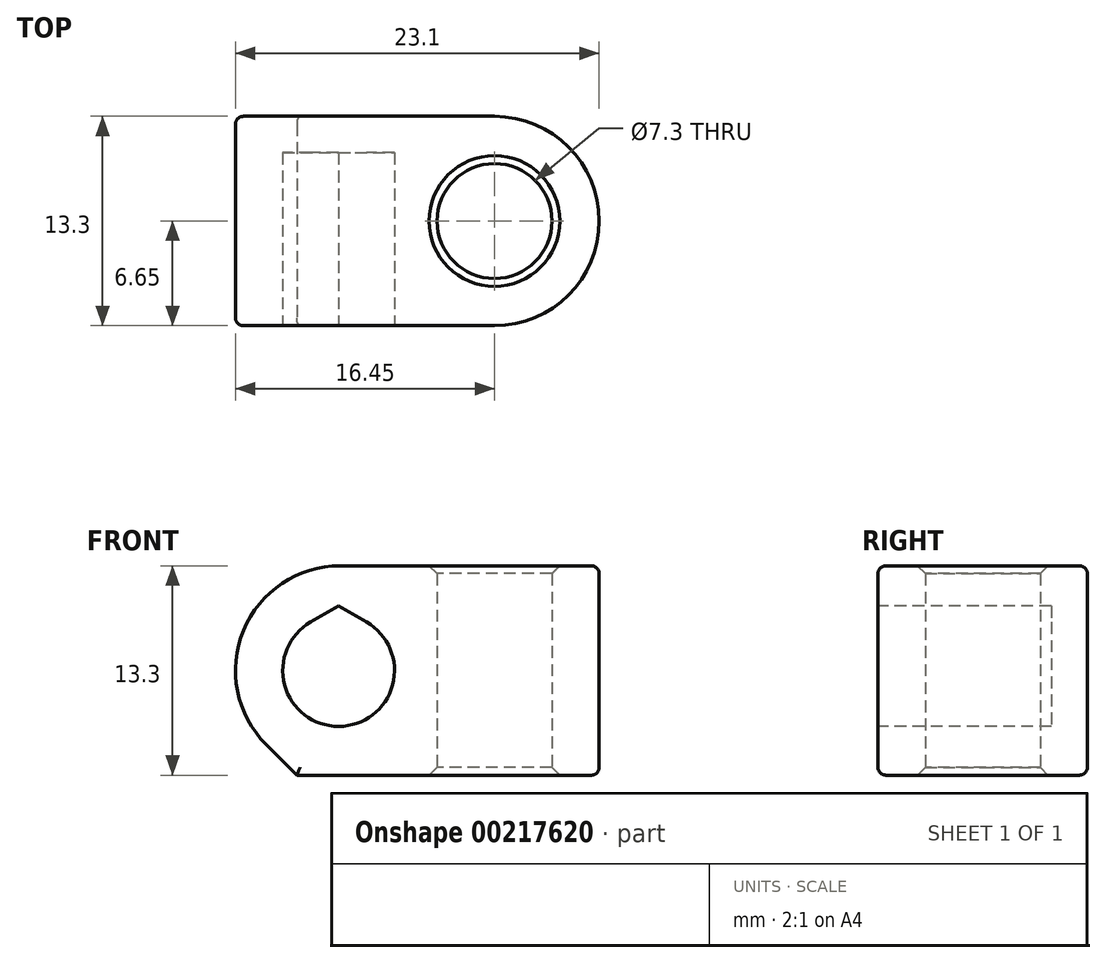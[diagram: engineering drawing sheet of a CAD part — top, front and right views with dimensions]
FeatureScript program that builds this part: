
annotation { "Feature Type Name" : "Feature", "Feature Type Description" : "" }
export const myFeature = defineFeature(function(context is Context, id is Id, definition is map)
    precondition{}
    {
        {
            var Q0;
            Q0=qCreatedBy(makeId("Top.planeOp"),FACE);
            var sketch = newSketch(context, id + "F0", { "sketchPlane" : qUnion([Q0])});
            skCircle(sketch, "E0", {"center": v(0, 0) * mm, "radius": 3.65 * mm});
            skLineSegment(sketch, "E1", {"start": v(-3.65, 0) * mm, "end": v(-6.15, 0) * mm, "construction": true});
            skCircle(sketch, "E2", {"center": v(-9.8, 0) * mm, "radius": 3.65 * mm});
            skLineSegment(sketch, "E3", {"start": v(0, 3.65) * mm, "end": v(0, 6.65) * mm, "construction": true});
            skLineSegment(sketch, "E4", {"start": v(0, 6.65) * mm, "end": v(-16.45, 6.65) * mm});
            skLineSegment(sketch, "E5", {"start": v(0, -6.65) * mm, "end": v(-16.45, -6.65) * mm});
            skLineSegment(sketch, "E6", {"start": v(-16.45, -6.65) * mm, "end": v(-16.45, 6.65) * mm});
            skLineSegment(sketch, "E7", {"start": v(-13.45, 0) * mm, "end": v(-16.45, 0) * mm, "construction": true});
            skArc(sketch, "E8.trimOffspring", {"start": v(0, -6.65) * mm, "mid": v(6.65, 0) * mm, "end": v(0, 6.65) * mm});
            skSolve(sketch);
        }
        {
            var Q0;
            Q0=makeQuery(id+"F0.imprint","IMPRINT",FACE,{"disambiguationData":[TD([[makeQuery(id+"F0.imprint","IMPRINT",EDGE,{"derivedFrom":sQuery(id+"F0.wireOp",EDGE,"E0")}),-1.0]])]});
            var Q1;
            Q1=makeQuery(id+"F0.imprint","IMPRINT",FACE,{"disambiguationData":[TD([[makeQuery(id+"F0.imprint","IMPRINT",EDGE,{"derivedFrom":sQuery(id+"F0.wireOp",EDGE,"E2")}),1.0]])]});
            extrude(context, id + "F1", {"entities" : qUnion([Q0, Q1]), "depth" : 13.3 * mm});
        }
        {
            var Q0;
            Q0=makeQuery(id+"F1.opExtrude","SWEPT_FACE",FACE,{"disambiguationData":[OSD([sQuery(id+"F0.wireOp",EDGE,"E5")])]});
            var sketch = newSketch(context, id + "F2", { "sketchPlane" : qUnion([Q0])});
            skLineSegment(sketch, "E9", {"start": v(-16.45, 6.65) * mm, "end": v(-13.45, 6.65) * mm, "construction": true});
            skArc(sketch, "E10", {"start": v(-11.67, 9.72) * mm, "mid": v(-9.9, 3.1) * mm, "end": v(-8.12, 9.72) * mm});
            skLineSegment(sketch, "E11", {"start": v(-9.9, 6.65) * mm, "end": v(-9.9, 10.75) * mm, "construction": true});
            skLineSegment(sketch, "E12", {"start": v(-9.9, 10.75) * mm, "end": v(-11.67, 9.72) * mm});
            skLineSegment(sketch, "E13", {"start": v(-9.9, 10.75) * mm, "end": v(-8.12, 9.72) * mm});
            skSolve(sketch);
        }
        {
            var Q0;
            Q0=makeQuery(id+"F2.imprint","IMPRINT",FACE,{"disambiguationData":[TD([[makeQuery(id+"F2.imprint","IMPRINT",EDGE,{"derivedFrom":sQuery(id+"F2.wireOp",EDGE,"E10")}),1.0]])]});
            extrude(context, id + "F3", {"entities" : qUnion([Q0]), "operationType" : NewBodyOperationType.REMOVE, "oppositeDirection" : true, "depth" : 11 * mm});
        }
        {
            var Q0;
            Q0=makeQuery(id+"F1.opExtrude","CAP_EDGE",EDGE,{"disambiguationData":[OSD([sQuery(id+"F0.wireOp",EDGE,"E6")])],"isStart":false});
            fillet(context, id + "F4", {"entities" : qUnion([Q0]), "radius" : 6.65 * mm, "tangentPropagation" : true, "allowEdgeOverflow" : false});
        }
        {
            var Q0;
            Q0=makeQuery(id+"F1.opExtrude","SWEPT_FACE",FACE,{"disambiguationData":[OSD([sQuery(id+"F0.wireOp",EDGE,"E5")])]});
            var sketch = newSketch(context, id + "F5", { "sketchPlane" : qUnion([Q0])});
            skLineSegment(sketch, "E14", {"start": v(-16.45, 6.65) * mm, "end": v(-16.45, 6.65) * mm});
            skLineSegment(sketch, "E15", {"start": v(-9.8, 0) * mm, "end": v(-3.62, 0) * mm});
            skPoint(sketch, "E16.visualSharp", {"position": v(-16.45, 0) * mm});
            skArc(sketch, "E16.filletArc", {"start": v(-16.45, 6.65) * mm, "mid": v(-15.94, 4.1) * mm, "end": v(-14.5, 1.95) * mm});
            skLineSegment(sketch, "E17", {"start": v(-14.5, 1.95) * mm, "end": v(-12.55, 0) * mm});
            skSolve(sketch);
        }
        {
            var Q0;
            Q0=makeQuery(id+"F5.imprint","IMPRINT",FACE,{"disambiguationData":[TD([[makeQuery(id+"F5.imprint","IMPRINT",EDGE,{"derivedFrom":sQuery(id+"F5.wireOp",EDGE,"E16.filletArc")}),-1.0]])]});
            extrude(context, id + "F6", {"entities" : qUnion([Q0]), "operationType" : NewBodyOperationType.REMOVE, "oppositeDirection" : true, "depth" : 25 * mm});
        }
        {
            var Q0;
            Q0=makeQuery(id+"F1.opExtrude","CAP_EDGE",EDGE,{"disambiguationData":[OSD([sQuery(id+"F0.wireOp",EDGE,"E5")])],"isStart":false});
            var Q1;
            Q1=makeQuery(id+"F1.opExtrude","CAP_EDGE",EDGE,{"disambiguationData":[OSD([sQuery(id+"F0.wireOp",EDGE,"E8.trimOffspring")])],"isStart":false});
            var Q2;
            Q2=makeQuery(id+"F1.opExtrude","CAP_EDGE",EDGE,{"disambiguationData":[OSD([sQuery(id+"F0.wireOp",EDGE,"E4")])],"isStart":false});
            var Q3;
            Q3=makeQuery(id+"F6.boolean.opBoolean","INTERSECT",EDGE,{"derivedFrom":[makeQuery(id+"F1.opExtrude","SWEPT_FACE",FACE,{"disambiguationData":[OSD([sQuery(id+"F0.wireOp",EDGE,"E4")])]}),makeQuery(id+"F6.opExtrude","SWEPT_FACE",FACE,{"disambiguationData":[OSD([sQuery(id+"F5.wireOp",EDGE,"E16.filletArc")])]})]});
            var Q4;
            Q4=makeQuery(id+"F6.boolean.opBoolean","COPY",EDGE,{"derivedFrom":makeQuery(id+"F6.opExtrude","SWEPT_EDGE",EDGE,{"disambiguationData":[OSD([sQuery(id+"F0.wireOp",EDGE,"E5"),sQuery(id+"F5.wireOp",EDGE,"E17")])]})});
            var Q5;
            Q5=makeQuery(id+"F6.boolean.opBoolean","COPY",EDGE,{"derivedFrom":makeQuery(id+"F6.opExtrude","CAP_EDGE",EDGE,{"disambiguationData":[OSD([sQuery(id+"F5.wireOp",EDGE,"E17")])],"isStart":true})});
            var Q6;
            Q6=makeQuery(id+"F1.opExtrude","CAP_EDGE",EDGE,{"disambiguationData":[OSD([sQuery(id+"F0.wireOp",EDGE,"E5")])],"isStart":true});
            var Q7;
            Q7=makeQuery(id+"F1.opExtrude","CAP_EDGE",EDGE,{"disambiguationData":[OSD([sQuery(id+"F0.wireOp",EDGE,"E8.trimOffspring")])],"isStart":true});
            fillet(context, id + "F7", {"entities" : qUnion([Q0, Q1, Q2, Q3, Q4, Q5, Q6, Q7]), "radius" : 0.5 * mm, "tangentPropagation" : true, "allowEdgeOverflow" : false});
        }
        {
            var Q0;
            Q0=makeQuery(id+"F3.boolean.opBoolean","COPY",EDGE,{"derivedFrom":makeQuery(id+"F3.opExtrude","CAP_EDGE",EDGE,{"disambiguationData":[OSD([sQuery(id+"F2.wireOp",EDGE,"E10")])],"isStart":true})});
            var Q1;
            Q1=makeQuery(id+"F3.boolean.opBoolean","INTERSECT",EDGE,{"derivedFrom":[makeQuery(id+"F1.opExtrude","SWEPT_FACE",FACE,{"disambiguationData":[OSD([sQuery(id+"F0.wireOp",EDGE,"E4")])]}),makeQuery(id+"F3.opExtrude","SWEPT_FACE",FACE,{"disambiguationData":[OSD([sQuery(id+"F2.wireOp",EDGE,"E10")])]})]});
            var Q2;
            Q2=makeQuery(id+"F1.opExtrude","CAP_EDGE",EDGE,{"disambiguationData":[OSD([sQuery(id+"F0.wireOp",EDGE,"E0")])],"isStart":false});
            var Q3;
            Q3=makeQuery(id+"F1.opExtrude","CAP_EDGE",EDGE,{"disambiguationData":[OSD([sQuery(id+"F0.wireOp",EDGE,"E0")])],"isStart":true});
            chamfer(context, id + "F8", {"entities" : qUnion([Q0, Q1, Q2, Q3]), "width" : 0.5 * mm, "tangentPropagation" : true});
        }
    });
